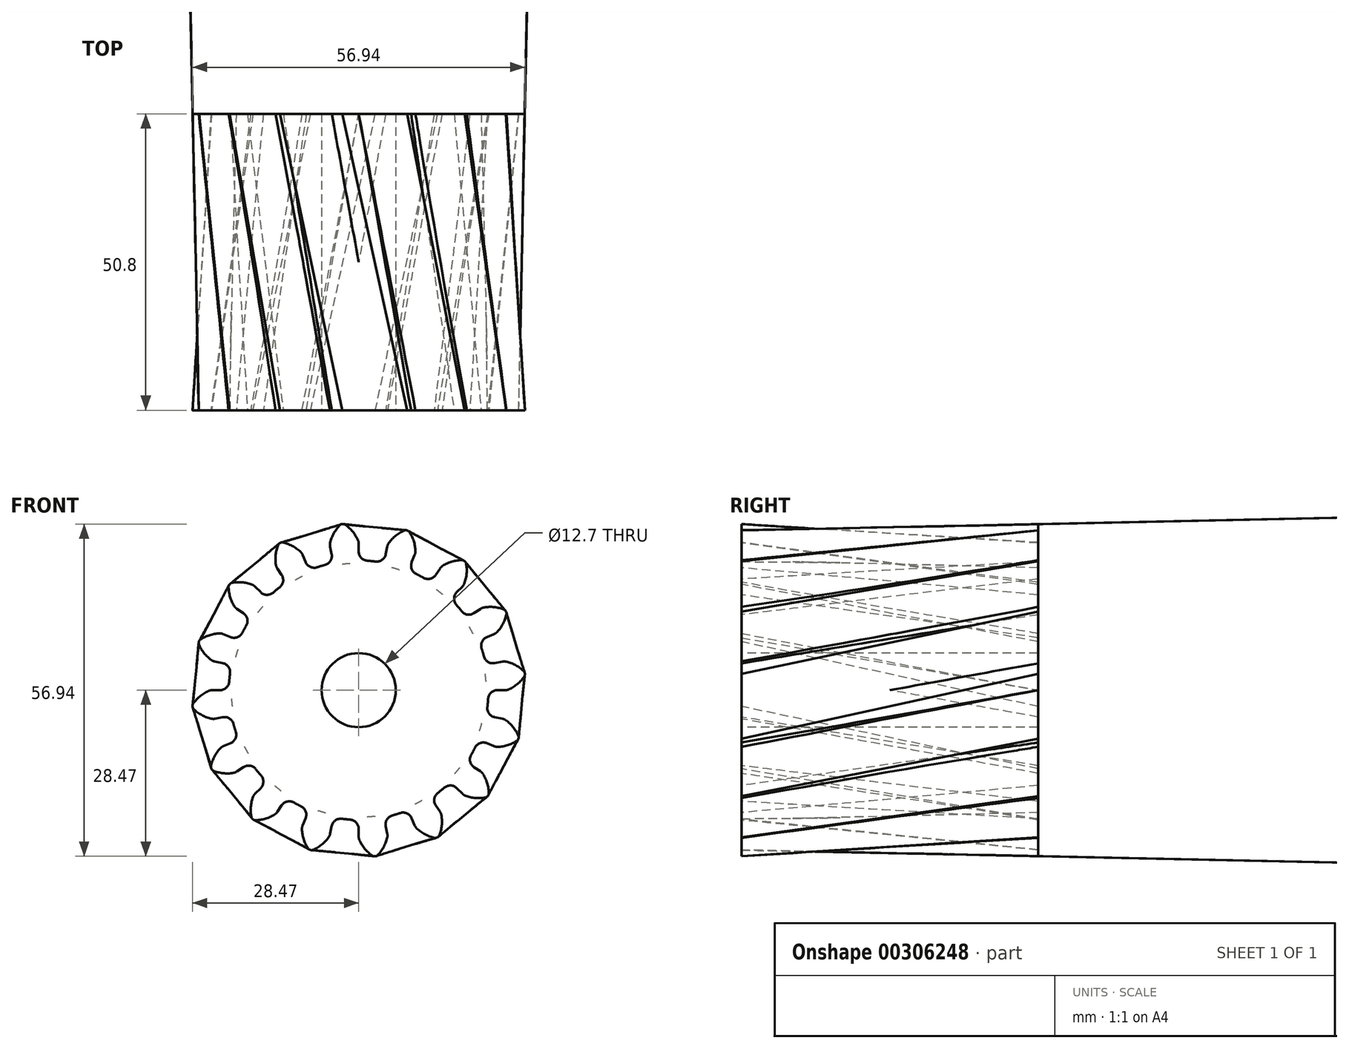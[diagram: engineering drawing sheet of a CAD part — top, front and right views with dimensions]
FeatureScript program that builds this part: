
annotation { "Feature Type Name" : "Feature", "Feature Type Description" : "" }
export const myFeature = defineFeature(function(context is Context, id is Id, definition is map)
    precondition{}
    {
        {
            var Q0;
            Q0=qCreatedBy(makeId("Front.planeOp"),FACE);
            var sketch = newSketch(context, id + "F0", { "sketchPlane" : qUnion([Q0])});
            skArc(sketch, "E0", {"start": v(-5.78, 21.46) * mm, "mid": v(-6.45, 21.27) * mm, "end": v(-7.12, 21.05) * mm});
            skArc(sketch, "E1.trimOffspring", {"start": v(-0.14, 25.74) * mm, "mid": v(-1.06, 27.2) * mm, "end": v(-2.34, 28.36) * mm});
            skLineSegment(sketch, "E2", {"start": v(-2.68, 28.45) * mm, "end": v(-2.8, 28.44) * mm});
            skLineSegment(sketch, "E3", {"start": v(0, 25.08) * mm, "end": v(0, 23.76) * mm});
            skLineSegment(sketch, "E4.MirrorCS", {"start": v(-4.9, 24.6) * mm, "end": v(-4.64, 23.3) * mm});
            skArc(sketch, "E5.MirrorCS", {"start": v(-4.88, 25.27) * mm, "mid": v(-4.27, 26.89) * mm, "end": v(-3.23, 28.28) * mm});
            skLineSegment(sketch, "E6.MirrorCS", {"start": v(-2.93, 28.43) * mm, "end": v(-2.8, 28.44) * mm});
            skPoint(sketch, "E7.visualSharp", {"position": v(-4.34, 21.8) * mm});
            skArc(sketch, "E7.filletArc", {"start": v(-5.78, 21.46) * mm, "mid": v(-4.84, 22.16) * mm, "end": v(-4.64, 23.3) * mm});
            skPoint(sketch, "E8.visualSharp", {"position": v(0, 22.23) * mm});
            skArc(sketch, "E8.filletArc", {"start": v(0, 23.76) * mm, "mid": v(0.43, 22.68) * mm, "end": v(1.48, 22.18) * mm});
            skPoint(sketch, "E9.visualSharp", {"position": v(-4.96, 24.91) * mm});
            skArc(sketch, "E9.filletArc", {"start": v(-4.88, 25.27) * mm, "mid": v(-4.92, 24.94) * mm, "end": v(-4.9, 24.6) * mm});
            skPoint(sketch, "E10.visualSharp", {"position": v(0, 25.4) * mm});
            skArc(sketch, "E10.filletArc", {"start": v(0, 25.08) * mm, "mid": v(-0.04, 25.42) * mm, "end": v(-0.14, 25.74) * mm});
            skPoint(sketch, "E11.visualSharp", {"position": v(-3.1, 28.4) * mm});
            skArc(sketch, "E11.filletArc", {"start": v(-2.93, 28.43) * mm, "mid": v(-3.1, 28.38) * mm, "end": v(-3.23, 28.28) * mm});
            skPoint(sketch, "E12.visualSharp", {"position": v(-2.5, 28.47) * mm});
            skArc(sketch, "E12.filletArc", {"start": v(-2.34, 28.36) * mm, "mid": v(-2.5, 28.44) * mm, "end": v(-2.68, 28.45) * mm});
            skPoint(sketch, "E13.1.0", {"position": v(-12.35, 18.48) * mm});
            skLineSegment(sketch, "E13.1.1", {"start": v(-9.6, 23.17) * mm, "end": v(-9.1, 21.95) * mm});
            skPoint(sketch, "E13.1.2", {"position": v(-13.2, 25.34) * mm});
            skArc(sketch, "E13.1.3", {"start": v(-14.18, 21.48) * mm, "mid": v(-14.23, 23.2) * mm, "end": v(-13.8, 24.89) * mm});
            skPoint(sketch, "E13.1.4", {"position": v(-13.74, 25.06) * mm});
            skPoint(sketch, "E13.1.5", {"position": v(-9.72, 23.47) * mm});
            skPoint(sketch, "E13.1.6", {"position": v(-14.11, 21.12) * mm});
            skPoint(sketch, "E13.1.7", {"position": v(-8.5, 20.53) * mm});
            skArc(sketch, "E13.1.8", {"start": v(-13.55, 17.62) * mm, "mid": v(-12.95, 18.62) * mm, "end": v(-13.2, 19.76) * mm});
            skArc(sketch, "E13.1.9", {"start": v(-9.98, 23.72) * mm, "mid": v(-11.4, 24.72) * mm, "end": v(-13.02, 25.3) * mm});
            skLineSegment(sketch, "E13.1.10", {"start": v(-13.94, 20.86) * mm, "end": v(-13.2, 19.76) * mm});
            skArc(sketch, "E13.1.11", {"start": v(-9.1, 21.95) * mm, "mid": v(-8.28, 21.11) * mm, "end": v(-7.12, 21.05) * mm});
            skArc(sketch, "E13.1.12", {"start": v(-14.18, 21.48) * mm, "mid": v(-14.1, 21.15) * mm, "end": v(-13.94, 20.86) * mm});
            skArc(sketch, "E13.1.13", {"start": v(-9.6, 23.17) * mm, "mid": v(-9.76, 23.47) * mm, "end": v(-9.98, 23.72) * mm});
            skArc(sketch, "E13.1.14", {"start": v(-13.58, 25.14) * mm, "mid": v(-13.72, 25.03) * mm, "end": v(-13.8, 24.89) * mm});
            skArc(sketch, "E13.1.15", {"start": v(-13.02, 25.3) * mm, "mid": v(-13.2, 25.31) * mm, "end": v(-13.36, 25.26) * mm});
            skLineSegment(sketch, "E13.1.16", {"start": v(-13.58, 25.14) * mm, "end": v(-13.47, 25.2) * mm});
            skLineSegment(sketch, "E13.1.17", {"start": v(-13.36, 25.26) * mm, "end": v(-13.47, 25.2) * mm});
            skPoint(sketch, "E13.2.0", {"position": v(-18.48, 12.35) * mm});
            skLineSegment(sketch, "E13.2.1", {"start": v(-17.74, 17.74) * mm, "end": v(-16.8, 16.8) * mm});
            skPoint(sketch, "E13.2.2", {"position": v(-21.9, 18.36) * mm});
            skArc(sketch, "E13.2.3", {"start": v(-21.32, 14.42) * mm, "mid": v(-22.03, 16) * mm, "end": v(-22.28, 17.7) * mm});
            skPoint(sketch, "E13.2.4", {"position": v(-22.28, 17.9) * mm});
            skPoint(sketch, "E13.2.5", {"position": v(-17.96, 17.96) * mm});
            skPoint(sketch, "E13.2.6", {"position": v(-21.12, 14.11) * mm});
            skPoint(sketch, "E13.2.7", {"position": v(-15.72, 15.72) * mm});
            skArc(sketch, "E13.2.8", {"start": v(-19.26, 11.09) * mm, "mid": v(-19.1, 12.24) * mm, "end": v(-19.76, 13.2) * mm});
            skArc(sketch, "E13.2.9", {"start": v(-18.3, 18.1) * mm, "mid": v(-19.99, 18.48) * mm, "end": v(-21.71, 18.4) * mm});
            skLineSegment(sketch, "E13.2.10", {"start": v(-20.86, 13.94) * mm, "end": v(-19.76, 13.2) * mm});
            skArc(sketch, "E13.2.11", {"start": v(-16.8, 16.8) * mm, "mid": v(-15.73, 16.34) * mm, "end": v(-14.63, 16.73) * mm});
            skArc(sketch, "E13.2.12", {"start": v(-21.32, 14.42) * mm, "mid": v(-21.11, 14.15) * mm, "end": v(-20.86, 13.94) * mm});
            skArc(sketch, "E13.2.13", {"start": v(-17.74, 17.74) * mm, "mid": v(-18, 17.95) * mm, "end": v(-18.3, 18.1) * mm});
            skArc(sketch, "E13.2.14", {"start": v(-22.17, 18.03) * mm, "mid": v(-22.25, 17.88) * mm, "end": v(-22.28, 17.7) * mm});
            skArc(sketch, "E13.2.15", {"start": v(-21.71, 18.4) * mm, "mid": v(-21.88, 18.34) * mm, "end": v(-22, 18.23) * mm});
            skLineSegment(sketch, "E13.2.16", {"start": v(-22.17, 18.03) * mm, "end": v(-22.1, 18.13) * mm});
            skLineSegment(sketch, "E13.2.17", {"start": v(-22, 18.23) * mm, "end": v(-22.1, 18.13) * mm});
            skLineSegment(sketch, "E14.1.3.0", {"start": v(-23.17, 9.6) * mm, "end": v(-21.95, 9.1) * mm});
            skPoint(sketch, "E14.4.3.0", {"position": v(-27.25, 8.59) * mm});
            skArc(sketch, "E14.5.3.0", {"start": v(-25.22, 5.16) * mm, "mid": v(-26.47, 6.35) * mm, "end": v(-27.36, 7.83) * mm});
            skPoint(sketch, "E14.9.3.0", {"position": v(-27.43, 8) * mm});
            skPoint(sketch, "E14.10.3.0", {"position": v(-23.47, 9.72) * mm});
            skPoint(sketch, "E14.11.3.0", {"position": v(-24.91, 4.96) * mm});
            skPoint(sketch, "E14.12.3.0", {"position": v(-20.53, 8.5) * mm});
            skArc(sketch, "E14.13.3.0", {"start": v(-22.04, 2.87) * mm, "mid": v(-22.32, 4) * mm, "end": v(-23.3, 4.64) * mm});
            skPoint(sketch, "E14.15.3.0", {"position": v(-21.8, 4.34) * mm});
            skArc(sketch, "E14.17.3.0", {"start": v(-23.83, 9.72) * mm, "mid": v(-25.54, 9.43) * mm, "end": v(-27.1, 8.69) * mm});
            skLineSegment(sketch, "E14.21.3.0", {"start": v(-24.6, 4.9) * mm, "end": v(-23.3, 4.64) * mm});
            skArc(sketch, "E14.24.3.0", {"start": v(-21.95, 9.1) * mm, "mid": v(-20.79, 9.07) * mm, "end": v(-19.92, 9.86) * mm});
            skArc(sketch, "E14.28.3.0", {"start": v(-25.22, 5.16) * mm, "mid": v(-24.92, 5) * mm, "end": v(-24.6, 4.9) * mm});
            skArc(sketch, "E14.32.3.0", {"start": v(-23.17, 9.6) * mm, "mid": v(-23.5, 9.7) * mm, "end": v(-23.83, 9.72) * mm});
            skArc(sketch, "E14.36.3.0", {"start": v(-27.38, 8.17) * mm, "mid": v(-27.4, 8) * mm, "end": v(-27.36, 7.83) * mm});
            skArc(sketch, "E14.40.3.0", {"start": v(-27.1, 8.69) * mm, "mid": v(-27.23, 8.57) * mm, "end": v(-27.3, 8.42) * mm});
            skLineSegment(sketch, "E14.44.3.0", {"start": v(-27.38, 8.17) * mm, "end": v(-27.35, 8.3) * mm});
            skLineSegment(sketch, "E14.47.3.0", {"start": v(-27.3, 8.42) * mm, "end": v(-27.35, 8.3) * mm});
            skLineSegment(sketch, "E14.1.4.0", {"start": v(-25.08, 0) * mm, "end": v(-23.76, 0) * mm});
            skPoint(sketch, "E14.4.4.0", {"position": v(-28.47, -2.5) * mm});
            skArc(sketch, "E14.5.4.0", {"start": v(-25.27, -4.88) * mm, "mid": v(-26.89, -4.27) * mm, "end": v(-28.28, -3.23) * mm});
            skPoint(sketch, "E14.9.4.0", {"position": v(-28.4, -3.1) * mm});
            skPoint(sketch, "E14.10.4.0", {"position": v(-25.4, 0) * mm});
            skPoint(sketch, "E14.11.4.0", {"position": v(-24.91, -4.96) * mm});
            skPoint(sketch, "E14.12.4.0", {"position": v(-22.23, 0) * mm});
            skArc(sketch, "E14.13.4.0", {"start": v(-21.46, -5.78) * mm, "mid": v(-22.16, -4.84) * mm, "end": v(-23.3, -4.64) * mm});
            skPoint(sketch, "E14.15.4.0", {"position": v(-21.8, -4.34) * mm});
            skArc(sketch, "E14.17.4.0", {"start": v(-25.74, -0.14) * mm, "mid": v(-27.2, -1.06) * mm, "end": v(-28.36, -2.34) * mm});
            skLineSegment(sketch, "E14.21.4.0", {"start": v(-24.6, -4.9) * mm, "end": v(-23.3, -4.64) * mm});
            skArc(sketch, "E14.24.4.0", {"start": v(-23.76, 0) * mm, "mid": v(-22.68, 0.43) * mm, "end": v(-22.18, 1.48) * mm});
            skArc(sketch, "E14.28.4.0", {"start": v(-25.27, -4.88) * mm, "mid": v(-24.94, -4.92) * mm, "end": v(-24.6, -4.9) * mm});
            skArc(sketch, "E14.32.4.0", {"start": v(-25.08, 0) * mm, "mid": v(-25.42, -0.04) * mm, "end": v(-25.74, -0.14) * mm});
            skArc(sketch, "E14.36.4.0", {"start": v(-28.43, -2.93) * mm, "mid": v(-28.38, -3.1) * mm, "end": v(-28.28, -3.23) * mm});
            skArc(sketch, "E14.40.4.0", {"start": v(-28.36, -2.34) * mm, "mid": v(-28.44, -2.5) * mm, "end": v(-28.45, -2.68) * mm});
            skLineSegment(sketch, "E14.44.4.0", {"start": v(-28.43, -2.93) * mm, "end": v(-28.44, -2.8) * mm});
            skLineSegment(sketch, "E14.47.4.0", {"start": v(-28.45, -2.68) * mm, "end": v(-28.44, -2.8) * mm});
            skLineSegment(sketch, "E14.1.5.0", {"start": v(-23.17, -9.6) * mm, "end": v(-21.95, -9.1) * mm});
            skPoint(sketch, "E14.4.5.0", {"position": v(-25.34, -13.2) * mm});
            skArc(sketch, "E14.5.5.0", {"start": v(-21.48, -14.18) * mm, "mid": v(-23.2, -14.23) * mm, "end": v(-24.89, -13.8) * mm});
            skPoint(sketch, "E14.9.5.0", {"position": v(-25.06, -13.74) * mm});
            skPoint(sketch, "E14.10.5.0", {"position": v(-23.47, -9.72) * mm});
            skPoint(sketch, "E14.11.5.0", {"position": v(-21.12, -14.11) * mm});
            skPoint(sketch, "E14.12.5.0", {"position": v(-20.53, -8.5) * mm});
            skArc(sketch, "E14.13.5.0", {"start": v(-17.62, -13.55) * mm, "mid": v(-18.62, -12.95) * mm, "end": v(-19.76, -13.2) * mm});
            skPoint(sketch, "E14.15.5.0", {"position": v(-18.48, -12.35) * mm});
            skArc(sketch, "E14.17.5.0", {"start": v(-23.72, -9.98) * mm, "mid": v(-24.72, -11.4) * mm, "end": v(-25.3, -13.02) * mm});
            skLineSegment(sketch, "E14.21.5.0", {"start": v(-20.86, -13.94) * mm, "end": v(-19.76, -13.2) * mm});
            skArc(sketch, "E14.24.5.0", {"start": v(-21.95, -9.1) * mm, "mid": v(-21.11, -8.28) * mm, "end": v(-21.05, -7.12) * mm});
            skArc(sketch, "E14.28.5.0", {"start": v(-21.48, -14.18) * mm, "mid": v(-21.15, -14.1) * mm, "end": v(-20.86, -13.94) * mm});
            skArc(sketch, "E14.32.5.0", {"start": v(-23.17, -9.6) * mm, "mid": v(-23.47, -9.76) * mm, "end": v(-23.72, -9.98) * mm});
            skArc(sketch, "E14.36.5.0", {"start": v(-25.14, -13.58) * mm, "mid": v(-25.03, -13.72) * mm, "end": v(-24.89, -13.8) * mm});
            skArc(sketch, "E14.40.5.0", {"start": v(-25.3, -13.02) * mm, "mid": v(-25.31, -13.2) * mm, "end": v(-25.26, -13.36) * mm});
            skLineSegment(sketch, "E14.44.5.0", {"start": v(-25.14, -13.58) * mm, "end": v(-25.2, -13.47) * mm});
            skLineSegment(sketch, "E14.47.5.0", {"start": v(-25.26, -13.36) * mm, "end": v(-25.2, -13.47) * mm});
            skLineSegment(sketch, "E14.1.6.0", {"start": v(-17.74, -17.74) * mm, "end": v(-16.8, -16.8) * mm});
            skPoint(sketch, "E14.4.6.0", {"position": v(-18.36, -21.9) * mm});
            skArc(sketch, "E14.5.6.0", {"start": v(-14.42, -21.32) * mm, "mid": v(-16, -22.03) * mm, "end": v(-17.7, -22.28) * mm});
            skPoint(sketch, "E14.9.6.0", {"position": v(-17.9, -22.28) * mm});
            skPoint(sketch, "E14.10.6.0", {"position": v(-17.96, -17.96) * mm});
            skPoint(sketch, "E14.11.6.0", {"position": v(-14.11, -21.12) * mm});
            skPoint(sketch, "E14.12.6.0", {"position": v(-15.72, -15.72) * mm});
            skArc(sketch, "E14.13.6.0", {"start": v(-11.09, -19.26) * mm, "mid": v(-12.24, -19.1) * mm, "end": v(-13.2, -19.76) * mm});
            skPoint(sketch, "E14.15.6.0", {"position": v(-12.35, -18.48) * mm});
            skArc(sketch, "E14.17.6.0", {"start": v(-18.1, -18.3) * mm, "mid": v(-18.48, -19.99) * mm, "end": v(-18.4, -21.71) * mm});
            skLineSegment(sketch, "E14.21.6.0", {"start": v(-13.94, -20.86) * mm, "end": v(-13.2, -19.76) * mm});
            skArc(sketch, "E14.24.6.0", {"start": v(-16.8, -16.8) * mm, "mid": v(-16.34, -15.73) * mm, "end": v(-16.73, -14.63) * mm});
            skArc(sketch, "E14.28.6.0", {"start": v(-14.42, -21.32) * mm, "mid": v(-14.15, -21.11) * mm, "end": v(-13.94, -20.86) * mm});
            skArc(sketch, "E14.32.6.0", {"start": v(-17.74, -17.74) * mm, "mid": v(-17.95, -18) * mm, "end": v(-18.1, -18.3) * mm});
            skArc(sketch, "E14.36.6.0", {"start": v(-18.03, -22.17) * mm, "mid": v(-17.88, -22.25) * mm, "end": v(-17.7, -22.28) * mm});
            skArc(sketch, "E14.40.6.0", {"start": v(-18.4, -21.71) * mm, "mid": v(-18.34, -21.88) * mm, "end": v(-18.23, -22) * mm});
            skLineSegment(sketch, "E14.44.6.0", {"start": v(-18.03, -22.17) * mm, "end": v(-18.13, -22.1) * mm});
            skLineSegment(sketch, "E14.47.6.0", {"start": v(-18.23, -22) * mm, "end": v(-18.13, -22.1) * mm});
            skLineSegment(sketch, "E14.1.7.0", {"start": v(-9.6, -23.17) * mm, "end": v(-9.1, -21.95) * mm});
            skPoint(sketch, "E14.4.7.0", {"position": v(-8.59, -27.25) * mm});
            skArc(sketch, "E14.5.7.0", {"start": v(-5.16, -25.22) * mm, "mid": v(-6.35, -26.47) * mm, "end": v(-7.83, -27.36) * mm});
            skPoint(sketch, "E14.9.7.0", {"position": v(-8, -27.43) * mm});
            skPoint(sketch, "E14.10.7.0", {"position": v(-9.72, -23.47) * mm});
            skPoint(sketch, "E14.11.7.0", {"position": v(-4.96, -24.91) * mm});
            skPoint(sketch, "E14.12.7.0", {"position": v(-8.5, -20.53) * mm});
            skArc(sketch, "E14.13.7.0", {"start": v(-2.87, -22.04) * mm, "mid": v(-4, -22.32) * mm, "end": v(-4.64, -23.3) * mm});
            skPoint(sketch, "E14.15.7.0", {"position": v(-4.34, -21.8) * mm});
            skArc(sketch, "E14.17.7.0", {"start": v(-9.72, -23.83) * mm, "mid": v(-9.43, -25.54) * mm, "end": v(-8.69, -27.1) * mm});
            skLineSegment(sketch, "E14.21.7.0", {"start": v(-4.9, -24.6) * mm, "end": v(-4.64, -23.3) * mm});
            skArc(sketch, "E14.24.7.0", {"start": v(-9.1, -21.95) * mm, "mid": v(-9.07, -20.79) * mm, "end": v(-9.86, -19.92) * mm});
            skArc(sketch, "E14.28.7.0", {"start": v(-5.16, -25.22) * mm, "mid": v(-5, -24.92) * mm, "end": v(-4.9, -24.6) * mm});
            skArc(sketch, "E14.32.7.0", {"start": v(-9.6, -23.17) * mm, "mid": v(-9.7, -23.5) * mm, "end": v(-9.72, -23.83) * mm});
            skArc(sketch, "E14.36.7.0", {"start": v(-8.17, -27.38) * mm, "mid": v(-8, -27.4) * mm, "end": v(-7.83, -27.36) * mm});
            skArc(sketch, "E14.40.7.0", {"start": v(-8.69, -27.1) * mm, "mid": v(-8.57, -27.23) * mm, "end": v(-8.42, -27.3) * mm});
            skLineSegment(sketch, "E14.44.7.0", {"start": v(-8.17, -27.38) * mm, "end": v(-8.3, -27.35) * mm});
            skLineSegment(sketch, "E14.47.7.0", {"start": v(-8.42, -27.3) * mm, "end": v(-8.3, -27.35) * mm});
            skLineSegment(sketch, "E14.1.8.0", {"start": v(0, -25.08) * mm, "end": v(0, -23.76) * mm});
            skPoint(sketch, "E14.4.8.0", {"position": v(2.5, -28.47) * mm});
            skArc(sketch, "E14.5.8.0", {"start": v(4.88, -25.27) * mm, "mid": v(4.27, -26.89) * mm, "end": v(3.23, -28.28) * mm});
            skPoint(sketch, "E14.9.8.0", {"position": v(3.1, -28.4) * mm});
            skPoint(sketch, "E14.10.8.0", {"position": v(0, -25.4) * mm});
            skPoint(sketch, "E14.11.8.0", {"position": v(4.96, -24.91) * mm});
            skPoint(sketch, "E14.12.8.0", {"position": v(0, -22.23) * mm});
            skArc(sketch, "E14.13.8.0", {"start": v(5.78, -21.46) * mm, "mid": v(4.84, -22.16) * mm, "end": v(4.64, -23.3) * mm});
            skPoint(sketch, "E14.15.8.0", {"position": v(4.34, -21.8) * mm});
            skArc(sketch, "E14.17.8.0", {"start": v(0.14, -25.74) * mm, "mid": v(1.06, -27.2) * mm, "end": v(2.34, -28.36) * mm});
            skLineSegment(sketch, "E14.21.8.0", {"start": v(4.9, -24.6) * mm, "end": v(4.64, -23.3) * mm});
            skArc(sketch, "E14.24.8.0", {"start": v(0, -23.76) * mm, "mid": v(-0.43, -22.68) * mm, "end": v(-1.48, -22.18) * mm});
            skArc(sketch, "E14.28.8.0", {"start": v(4.88, -25.27) * mm, "mid": v(4.92, -24.94) * mm, "end": v(4.9, -24.6) * mm});
            skArc(sketch, "E14.32.8.0", {"start": v(0, -25.08) * mm, "mid": v(0.04, -25.42) * mm, "end": v(0.14, -25.74) * mm});
            skArc(sketch, "E14.36.8.0", {"start": v(2.93, -28.43) * mm, "mid": v(3.1, -28.38) * mm, "end": v(3.23, -28.28) * mm});
            skArc(sketch, "E14.40.8.0", {"start": v(2.34, -28.36) * mm, "mid": v(2.5, -28.44) * mm, "end": v(2.68, -28.45) * mm});
            skLineSegment(sketch, "E14.44.8.0", {"start": v(2.93, -28.43) * mm, "end": v(2.8, -28.44) * mm});
            skLineSegment(sketch, "E14.47.8.0", {"start": v(2.68, -28.45) * mm, "end": v(2.8, -28.44) * mm});
            skLineSegment(sketch, "E14.1.9.0", {"start": v(9.6, -23.17) * mm, "end": v(9.1, -21.95) * mm});
            skPoint(sketch, "E14.4.9.0", {"position": v(13.2, -25.34) * mm});
            skArc(sketch, "E14.5.9.0", {"start": v(14.18, -21.48) * mm, "mid": v(14.23, -23.2) * mm, "end": v(13.8, -24.89) * mm});
            skPoint(sketch, "E14.9.9.0", {"position": v(13.74, -25.06) * mm});
            skPoint(sketch, "E14.10.9.0", {"position": v(9.72, -23.47) * mm});
            skPoint(sketch, "E14.11.9.0", {"position": v(14.11, -21.12) * mm});
            skPoint(sketch, "E14.12.9.0", {"position": v(8.5, -20.53) * mm});
            skArc(sketch, "E14.13.9.0", {"start": v(13.55, -17.62) * mm, "mid": v(12.95, -18.62) * mm, "end": v(13.2, -19.76) * mm});
            skPoint(sketch, "E14.15.9.0", {"position": v(12.35, -18.48) * mm});
            skArc(sketch, "E14.17.9.0", {"start": v(9.98, -23.72) * mm, "mid": v(11.4, -24.72) * mm, "end": v(13.02, -25.3) * mm});
            skLineSegment(sketch, "E14.21.9.0", {"start": v(13.94, -20.86) * mm, "end": v(13.2, -19.76) * mm});
            skArc(sketch, "E14.24.9.0", {"start": v(9.1, -21.95) * mm, "mid": v(8.28, -21.11) * mm, "end": v(7.12, -21.05) * mm});
            skArc(sketch, "E14.28.9.0", {"start": v(14.18, -21.48) * mm, "mid": v(14.1, -21.15) * mm, "end": v(13.94, -20.86) * mm});
            skArc(sketch, "E14.32.9.0", {"start": v(9.6, -23.17) * mm, "mid": v(9.76, -23.47) * mm, "end": v(9.98, -23.72) * mm});
            skArc(sketch, "E14.36.9.0", {"start": v(13.58, -25.14) * mm, "mid": v(13.72, -25.03) * mm, "end": v(13.8, -24.89) * mm});
            skArc(sketch, "E14.40.9.0", {"start": v(13.02, -25.3) * mm, "mid": v(13.2, -25.31) * mm, "end": v(13.36, -25.26) * mm});
            skLineSegment(sketch, "E14.44.9.0", {"start": v(13.58, -25.14) * mm, "end": v(13.47, -25.2) * mm});
            skLineSegment(sketch, "E14.47.9.0", {"start": v(13.36, -25.26) * mm, "end": v(13.47, -25.2) * mm});
            skLineSegment(sketch, "E14.1.10.0", {"start": v(17.74, -17.74) * mm, "end": v(16.8, -16.8) * mm});
            skPoint(sketch, "E14.4.10.0", {"position": v(21.9, -18.36) * mm});
            skArc(sketch, "E14.5.10.0", {"start": v(21.32, -14.42) * mm, "mid": v(22.03, -16) * mm, "end": v(22.28, -17.7) * mm});
            skPoint(sketch, "E14.9.10.0", {"position": v(22.28, -17.9) * mm});
            skPoint(sketch, "E14.10.10.0", {"position": v(17.96, -17.96) * mm});
            skPoint(sketch, "E14.11.10.0", {"position": v(21.12, -14.11) * mm});
            skPoint(sketch, "E14.12.10.0", {"position": v(15.72, -15.72) * mm});
            skArc(sketch, "E14.13.10.0", {"start": v(19.26, -11.09) * mm, "mid": v(19.1, -12.24) * mm, "end": v(19.76, -13.2) * mm});
            skPoint(sketch, "E14.15.10.0", {"position": v(18.48, -12.35) * mm});
            skArc(sketch, "E14.17.10.0", {"start": v(18.3, -18.1) * mm, "mid": v(19.99, -18.48) * mm, "end": v(21.71, -18.4) * mm});
            skLineSegment(sketch, "E14.21.10.0", {"start": v(20.86, -13.94) * mm, "end": v(19.76, -13.2) * mm});
            skArc(sketch, "E14.24.10.0", {"start": v(16.8, -16.8) * mm, "mid": v(15.73, -16.34) * mm, "end": v(14.63, -16.73) * mm});
            skArc(sketch, "E14.28.10.0", {"start": v(21.32, -14.42) * mm, "mid": v(21.11, -14.15) * mm, "end": v(20.86, -13.94) * mm});
            skArc(sketch, "E14.32.10.0", {"start": v(17.74, -17.74) * mm, "mid": v(18, -17.95) * mm, "end": v(18.3, -18.1) * mm});
            skArc(sketch, "E14.36.10.0", {"start": v(22.17, -18.03) * mm, "mid": v(22.25, -17.88) * mm, "end": v(22.28, -17.7) * mm});
            skArc(sketch, "E14.40.10.0", {"start": v(21.71, -18.4) * mm, "mid": v(21.88, -18.34) * mm, "end": v(22, -18.23) * mm});
            skLineSegment(sketch, "E14.44.10.0", {"start": v(22.17, -18.03) * mm, "end": v(22.1, -18.13) * mm});
            skLineSegment(sketch, "E14.47.10.0", {"start": v(22, -18.23) * mm, "end": v(22.1, -18.13) * mm});
            skLineSegment(sketch, "E14.1.11.0", {"start": v(23.17, -9.6) * mm, "end": v(21.95, -9.1) * mm});
            skPoint(sketch, "E14.4.11.0", {"position": v(27.25, -8.59) * mm});
            skArc(sketch, "E14.5.11.0", {"start": v(25.22, -5.16) * mm, "mid": v(26.47, -6.35) * mm, "end": v(27.36, -7.83) * mm});
            skPoint(sketch, "E14.9.11.0", {"position": v(27.43, -8) * mm});
            skPoint(sketch, "E14.10.11.0", {"position": v(23.47, -9.72) * mm});
            skPoint(sketch, "E14.11.11.0", {"position": v(24.91, -4.96) * mm});
            skPoint(sketch, "E14.12.11.0", {"position": v(20.53, -8.5) * mm});
            skArc(sketch, "E14.13.11.0", {"start": v(22.04, -2.87) * mm, "mid": v(22.32, -4) * mm, "end": v(23.3, -4.64) * mm});
            skPoint(sketch, "E14.15.11.0", {"position": v(21.8, -4.34) * mm});
            skArc(sketch, "E14.17.11.0", {"start": v(23.83, -9.72) * mm, "mid": v(25.54, -9.43) * mm, "end": v(27.1, -8.69) * mm});
            skLineSegment(sketch, "E14.21.11.0", {"start": v(24.6, -4.9) * mm, "end": v(23.3, -4.64) * mm});
            skArc(sketch, "E14.24.11.0", {"start": v(21.95, -9.1) * mm, "mid": v(20.79, -9.07) * mm, "end": v(19.92, -9.86) * mm});
            skArc(sketch, "E14.28.11.0", {"start": v(25.22, -5.16) * mm, "mid": v(24.92, -5) * mm, "end": v(24.6, -4.9) * mm});
            skArc(sketch, "E14.32.11.0", {"start": v(23.17, -9.6) * mm, "mid": v(23.5, -9.7) * mm, "end": v(23.83, -9.72) * mm});
            skArc(sketch, "E14.36.11.0", {"start": v(27.38, -8.17) * mm, "mid": v(27.4, -8) * mm, "end": v(27.36, -7.83) * mm});
            skArc(sketch, "E14.40.11.0", {"start": v(27.1, -8.69) * mm, "mid": v(27.23, -8.57) * mm, "end": v(27.3, -8.42) * mm});
            skLineSegment(sketch, "E14.44.11.0", {"start": v(27.38, -8.17) * mm, "end": v(27.35, -8.3) * mm});
            skLineSegment(sketch, "E14.47.11.0", {"start": v(27.3, -8.42) * mm, "end": v(27.35, -8.3) * mm});
            skLineSegment(sketch, "E14.1.12.0", {"start": v(25.08, 0) * mm, "end": v(23.76, 0) * mm});
            skPoint(sketch, "E14.4.12.0", {"position": v(28.47, 2.5) * mm});
            skArc(sketch, "E14.5.12.0", {"start": v(25.27, 4.88) * mm, "mid": v(26.89, 4.27) * mm, "end": v(28.28, 3.23) * mm});
            skPoint(sketch, "E14.9.12.0", {"position": v(28.4, 3.1) * mm});
            skPoint(sketch, "E14.10.12.0", {"position": v(25.4, 0) * mm});
            skPoint(sketch, "E14.11.12.0", {"position": v(24.91, 4.96) * mm});
            skPoint(sketch, "E14.12.12.0", {"position": v(22.23, 0) * mm});
            skArc(sketch, "E14.13.12.0", {"start": v(21.46, 5.78) * mm, "mid": v(22.16, 4.84) * mm, "end": v(23.3, 4.64) * mm});
            skPoint(sketch, "E14.15.12.0", {"position": v(21.8, 4.34) * mm});
            skArc(sketch, "E14.17.12.0", {"start": v(25.74, 0.14) * mm, "mid": v(27.2, 1.06) * mm, "end": v(28.36, 2.34) * mm});
            skLineSegment(sketch, "E14.21.12.0", {"start": v(24.6, 4.9) * mm, "end": v(23.3, 4.64) * mm});
            skArc(sketch, "E14.24.12.0", {"start": v(23.76, 0) * mm, "mid": v(22.68, -0.43) * mm, "end": v(22.18, -1.48) * mm});
            skArc(sketch, "E14.28.12.0", {"start": v(25.27, 4.88) * mm, "mid": v(24.94, 4.92) * mm, "end": v(24.6, 4.9) * mm});
            skArc(sketch, "E14.32.12.0", {"start": v(25.08, 0) * mm, "mid": v(25.42, 0.04) * mm, "end": v(25.74, 0.14) * mm});
            skArc(sketch, "E14.36.12.0", {"start": v(28.43, 2.93) * mm, "mid": v(28.38, 3.1) * mm, "end": v(28.28, 3.23) * mm});
            skArc(sketch, "E14.40.12.0", {"start": v(28.36, 2.34) * mm, "mid": v(28.44, 2.5) * mm, "end": v(28.45, 2.68) * mm});
            skLineSegment(sketch, "E14.44.12.0", {"start": v(28.43, 2.93) * mm, "end": v(28.44, 2.8) * mm});
            skLineSegment(sketch, "E14.47.12.0", {"start": v(28.45, 2.68) * mm, "end": v(28.44, 2.8) * mm});
            skLineSegment(sketch, "E14.1.13.0", {"start": v(23.17, 9.6) * mm, "end": v(21.95, 9.1) * mm});
            skPoint(sketch, "E14.4.13.0", {"position": v(25.34, 13.2) * mm});
            skArc(sketch, "E14.5.13.0", {"start": v(21.48, 14.18) * mm, "mid": v(23.2, 14.23) * mm, "end": v(24.89, 13.8) * mm});
            skPoint(sketch, "E14.9.13.0", {"position": v(25.06, 13.74) * mm});
            skPoint(sketch, "E14.10.13.0", {"position": v(23.47, 9.72) * mm});
            skPoint(sketch, "E14.11.13.0", {"position": v(21.12, 14.11) * mm});
            skPoint(sketch, "E14.12.13.0", {"position": v(20.53, 8.5) * mm});
            skArc(sketch, "E14.13.13.0", {"start": v(17.62, 13.55) * mm, "mid": v(18.62, 12.95) * mm, "end": v(19.76, 13.2) * mm});
            skPoint(sketch, "E14.15.13.0", {"position": v(18.48, 12.35) * mm});
            skArc(sketch, "E14.17.13.0", {"start": v(23.72, 9.98) * mm, "mid": v(24.72, 11.4) * mm, "end": v(25.3, 13.02) * mm});
            skLineSegment(sketch, "E14.21.13.0", {"start": v(20.86, 13.94) * mm, "end": v(19.76, 13.2) * mm});
            skArc(sketch, "E14.24.13.0", {"start": v(21.95, 9.1) * mm, "mid": v(21.11, 8.28) * mm, "end": v(21.05, 7.12) * mm});
            skArc(sketch, "E14.28.13.0", {"start": v(21.48, 14.18) * mm, "mid": v(21.15, 14.1) * mm, "end": v(20.86, 13.94) * mm});
            skArc(sketch, "E14.32.13.0", {"start": v(23.17, 9.6) * mm, "mid": v(23.47, 9.76) * mm, "end": v(23.72, 9.98) * mm});
            skArc(sketch, "E14.36.13.0", {"start": v(25.14, 13.58) * mm, "mid": v(25.03, 13.72) * mm, "end": v(24.89, 13.8) * mm});
            skArc(sketch, "E14.40.13.0", {"start": v(25.3, 13.02) * mm, "mid": v(25.31, 13.2) * mm, "end": v(25.26, 13.36) * mm});
            skLineSegment(sketch, "E14.44.13.0", {"start": v(25.14, 13.58) * mm, "end": v(25.2, 13.47) * mm});
            skLineSegment(sketch, "E14.47.13.0", {"start": v(25.26, 13.36) * mm, "end": v(25.2, 13.47) * mm});
            skLineSegment(sketch, "E14.1.14.0", {"start": v(17.74, 17.74) * mm, "end": v(16.8, 16.8) * mm});
            skPoint(sketch, "E14.4.14.0", {"position": v(18.36, 21.9) * mm});
            skArc(sketch, "E14.5.14.0", {"start": v(14.42, 21.32) * mm, "mid": v(16, 22.03) * mm, "end": v(17.7, 22.28) * mm});
            skPoint(sketch, "E14.9.14.0", {"position": v(17.9, 22.28) * mm});
            skPoint(sketch, "E14.10.14.0", {"position": v(17.96, 17.96) * mm});
            skPoint(sketch, "E14.11.14.0", {"position": v(14.11, 21.12) * mm});
            skPoint(sketch, "E14.12.14.0", {"position": v(15.72, 15.72) * mm});
            skArc(sketch, "E14.13.14.0", {"start": v(11.09, 19.26) * mm, "mid": v(12.24, 19.1) * mm, "end": v(13.2, 19.76) * mm});
            skPoint(sketch, "E14.15.14.0", {"position": v(12.35, 18.48) * mm});
            skArc(sketch, "E14.17.14.0", {"start": v(18.1, 18.3) * mm, "mid": v(18.48, 19.99) * mm, "end": v(18.4, 21.71) * mm});
            skLineSegment(sketch, "E14.21.14.0", {"start": v(13.94, 20.86) * mm, "end": v(13.2, 19.76) * mm});
            skArc(sketch, "E14.24.14.0", {"start": v(16.8, 16.8) * mm, "mid": v(16.34, 15.73) * mm, "end": v(16.73, 14.63) * mm});
            skArc(sketch, "E14.28.14.0", {"start": v(14.42, 21.32) * mm, "mid": v(14.15, 21.11) * mm, "end": v(13.94, 20.86) * mm});
            skArc(sketch, "E14.32.14.0", {"start": v(17.74, 17.74) * mm, "mid": v(17.95, 18) * mm, "end": v(18.1, 18.3) * mm});
            skArc(sketch, "E14.36.14.0", {"start": v(18.03, 22.17) * mm, "mid": v(17.88, 22.25) * mm, "end": v(17.7, 22.28) * mm});
            skArc(sketch, "E14.40.14.0", {"start": v(18.4, 21.71) * mm, "mid": v(18.34, 21.88) * mm, "end": v(18.23, 22) * mm});
            skLineSegment(sketch, "E14.44.14.0", {"start": v(18.03, 22.17) * mm, "end": v(18.13, 22.1) * mm});
            skLineSegment(sketch, "E14.47.14.0", {"start": v(18.23, 22) * mm, "end": v(18.13, 22.1) * mm});
            skLineSegment(sketch, "E14.1.15.0", {"start": v(9.6, 23.17) * mm, "end": v(9.1, 21.95) * mm});
            skPoint(sketch, "E14.4.15.0", {"position": v(8.59, 27.25) * mm});
            skArc(sketch, "E14.5.15.0", {"start": v(5.16, 25.22) * mm, "mid": v(6.35, 26.47) * mm, "end": v(7.83, 27.36) * mm});
            skPoint(sketch, "E14.9.15.0", {"position": v(8, 27.43) * mm});
            skPoint(sketch, "E14.10.15.0", {"position": v(9.72, 23.47) * mm});
            skPoint(sketch, "E14.11.15.0", {"position": v(4.96, 24.91) * mm});
            skPoint(sketch, "E14.12.15.0", {"position": v(8.5, 20.53) * mm});
            skArc(sketch, "E14.13.15.0", {"start": v(2.87, 22.04) * mm, "mid": v(4, 22.32) * mm, "end": v(4.64, 23.3) * mm});
            skPoint(sketch, "E14.15.15.0", {"position": v(4.34, 21.8) * mm});
            skArc(sketch, "E14.17.15.0", {"start": v(9.72, 23.83) * mm, "mid": v(9.43, 25.54) * mm, "end": v(8.69, 27.1) * mm});
            skLineSegment(sketch, "E14.21.15.0", {"start": v(4.9, 24.6) * mm, "end": v(4.64, 23.3) * mm});
            skArc(sketch, "E14.24.15.0", {"start": v(9.1, 21.95) * mm, "mid": v(9.07, 20.79) * mm, "end": v(9.86, 19.92) * mm});
            skArc(sketch, "E14.28.15.0", {"start": v(5.16, 25.22) * mm, "mid": v(5, 24.92) * mm, "end": v(4.9, 24.6) * mm});
            skArc(sketch, "E14.32.15.0", {"start": v(9.6, 23.17) * mm, "mid": v(9.7, 23.5) * mm, "end": v(9.72, 23.83) * mm});
            skArc(sketch, "E14.36.15.0", {"start": v(8.17, 27.38) * mm, "mid": v(8, 27.4) * mm, "end": v(7.83, 27.36) * mm});
            skArc(sketch, "E14.40.15.0", {"start": v(8.69, 27.1) * mm, "mid": v(8.57, 27.23) * mm, "end": v(8.42, 27.3) * mm});
            skLineSegment(sketch, "E14.44.15.0", {"start": v(8.17, 27.38) * mm, "end": v(8.3, 27.35) * mm});
            skLineSegment(sketch, "E14.47.15.0", {"start": v(8.42, 27.3) * mm, "end": v(8.3, 27.35) * mm});
            skArc(sketch, "E15.trimOffspring", {"start": v(2.87, 22.04) * mm, "mid": v(2.18, 22.12) * mm, "end": v(1.48, 22.18) * mm});
            skArc(sketch, "E16.trimOffspring", {"start": v(12.35, 18.48) * mm, "mid": v(11.12, 19.24) * mm, "end": v(9.86, 19.92) * mm});
            skArc(sketch, "E17.trimOffspring", {"start": v(17.62, 13.55) * mm, "mid": v(17.18, 14.1) * mm, "end": v(16.73, 14.63) * mm});
            skArc(sketch, "E18.trimOffspring", {"start": v(21.46, 5.78) * mm, "mid": v(21.27, 6.45) * mm, "end": v(21.05, 7.12) * mm});
            skArc(sketch, "E19.trimOffspring", {"start": v(22.04, -2.87) * mm, "mid": v(22.12, -2.18) * mm, "end": v(22.18, -1.48) * mm});
            skArc(sketch, "E20.trimOffspring", {"start": v(19.26, -11.09) * mm, "mid": v(19.6, -10.48) * mm, "end": v(19.92, -9.86) * mm});
            skArc(sketch, "E21.trimOffspring", {"start": v(13.55, -17.62) * mm, "mid": v(14.1, -17.18) * mm, "end": v(14.63, -16.73) * mm});
            skArc(sketch, "E22.trimOffspring", {"start": v(5.78, -21.46) * mm, "mid": v(6.45, -21.27) * mm, "end": v(7.12, -21.05) * mm});
            skArc(sketch, "E23.trimOffspring", {"start": v(-2.87, -22.04) * mm, "mid": v(-2.18, -22.12) * mm, "end": v(-1.48, -22.18) * mm});
            skArc(sketch, "E24.trimOffspring", {"start": v(-11.09, -19.26) * mm, "mid": v(-10.48, -19.6) * mm, "end": v(-9.86, -19.92) * mm});
            skArc(sketch, "E25.trimOffspring", {"start": v(-17.62, -13.55) * mm, "mid": v(-17.18, -14.1) * mm, "end": v(-16.73, -14.63) * mm});
            skArc(sketch, "E26.trimOffspring", {"start": v(-21.46, -5.78) * mm, "mid": v(-21.27, -6.45) * mm, "end": v(-21.05, -7.12) * mm});
            skArc(sketch, "E27.trimOffspring", {"start": v(-22.04, 2.87) * mm, "mid": v(-22.12, 2.18) * mm, "end": v(-22.18, 1.48) * mm});
            skArc(sketch, "E28.trimOffspring", {"start": v(-19.26, 11.09) * mm, "mid": v(-19.6, 10.48) * mm, "end": v(-19.92, 9.86) * mm});
            skArc(sketch, "E29.trimOffspring", {"start": v(-13.55, 17.62) * mm, "mid": v(-14.1, 17.18) * mm, "end": v(-14.63, 16.73) * mm});
            skSolve(sketch);
        }
        {
            var Q0;
            Q0=qCreatedBy(makeId("Front.planeOp"),FACE);
            cPlane(context, id + "F1", {"entities" : qUnion([Q0]), "cplaneType" : CPlaneType.OFFSET, "offset" : 50.8 * mm, "width" : 152.4 * mm, "height" : 152.4 * mm});
        }
        {
            var Q0;
            Q0=qCreatedBy(id+"F1.planeOp",FACE);
            var sketch = newSketch(context, id + "F2", { "sketchPlane" : qUnion([Q0])});
            skArc(sketch, "E30", {"start": v(-5.78, 21.46) * mm, "mid": v(-6.45, 21.27) * mm, "end": v(-7.12, 21.05) * mm});
            skArc(sketch, "E31.trimOffspring", {"start": v(-0.14, 25.74) * mm, "mid": v(-1.07, 27.21) * mm, "end": v(-2.37, 28.38) * mm});
            skLineSegment(sketch, "E32", {"start": v(-2.65, 28.47) * mm, "end": v(-2.8, 28.47) * mm});
            skLineSegment(sketch, "E33", {"start": v(0, 25.08) * mm, "end": v(0, 23.76) * mm});
            skLineSegment(sketch, "E34.MirrorCS", {"start": v(-2.95, 28.44) * mm, "end": v(-2.8, 28.47) * mm});
            skArc(sketch, "E35.MirrorCS", {"start": v(-4.88, 25.27) * mm, "mid": v(-4.26, 26.9) * mm, "end": v(-3.22, 28.3) * mm});
            skLineSegment(sketch, "E36.MirrorCS", {"start": v(-4.9, 24.6) * mm, "end": v(-4.64, 23.3) * mm});
            skPoint(sketch, "E37.visualSharp", {"position": v(-4.34, 21.8) * mm});
            skArc(sketch, "E37.filletArc", {"start": v(-4.7, 21.72) * mm, "mid": v(-4.46, 21.88) * mm, "end": v(-4.4, 22.16) * mm});
            skArc(sketch, "E38.filletArc", {"start": v(-5.78, 21.46) * mm, "mid": v(-4.84, 22.16) * mm, "end": v(-4.64, 23.3) * mm});
            skPoint(sketch, "E39.visualSharp", {"position": v(0, 22.23) * mm});
            skArc(sketch, "E39.filletArc", {"start": v(0, 23.76) * mm, "mid": v(0.43, 22.68) * mm, "end": v(1.48, 22.18) * mm});
            skPoint(sketch, "E40.visualSharp", {"position": v(-4.96, 24.91) * mm});
            skArc(sketch, "E40.filletArc", {"start": v(-4.88, 25.27) * mm, "mid": v(-4.92, 24.94) * mm, "end": v(-4.9, 24.6) * mm});
            skPoint(sketch, "E41.visualSharp", {"position": v(0, 25.4) * mm});
            skArc(sketch, "E41.filletArc", {"start": v(0, 25.08) * mm, "mid": v(-0.04, 25.42) * mm, "end": v(-0.14, 25.74) * mm});
            skPoint(sketch, "E42.visualSharp", {"position": v(-3.1, 28.4) * mm});
            skArc(sketch, "E42.filletArc", {"start": v(-2.95, 28.44) * mm, "mid": v(-3.1, 28.38) * mm, "end": v(-3.22, 28.3) * mm});
            skPoint(sketch, "E43.visualSharp", {"position": v(-2.5, 28.47) * mm});
            skArc(sketch, "E43.filletArc", {"start": v(-2.37, 28.38) * mm, "mid": v(-2.5, 28.44) * mm, "end": v(-2.65, 28.47) * mm});
            skArc(sketch, "E44.1.0", {"start": v(-13.55, 17.62) * mm, "mid": v(-12.95, 18.62) * mm, "end": v(-13.2, 19.76) * mm});
            skArc(sketch, "E44.1.1", {"start": v(-9.1, 21.95) * mm, "mid": v(-8.28, 21.11) * mm, "end": v(-7.12, 21.05) * mm});
            skPoint(sketch, "E44.1.2", {"position": v(-13.74, 25.06) * mm});
            skPoint(sketch, "E44.1.3", {"position": v(-14.11, 21.12) * mm});
            skPoint(sketch, "E44.1.4", {"position": v(-9.72, 23.47) * mm});
            skPoint(sketch, "E44.1.5", {"position": v(-13.2, 25.34) * mm});
            skLineSegment(sketch, "E44.1.6", {"start": v(-9.6, 23.17) * mm, "end": v(-9.1, 21.95) * mm});
            skArc(sketch, "E44.1.7", {"start": v(-9.98, 23.72) * mm, "mid": v(-11.4, 24.73) * mm, "end": v(-13.05, 25.31) * mm});
            skArc(sketch, "E44.1.8", {"start": v(-14.18, 21.48) * mm, "mid": v(-14.23, 23.22) * mm, "end": v(-13.8, 24.9) * mm});
            skLineSegment(sketch, "E44.1.9", {"start": v(-13.94, 20.86) * mm, "end": v(-13.2, 19.76) * mm});
            skArc(sketch, "E44.1.10", {"start": v(-9.6, 23.17) * mm, "mid": v(-9.76, 23.47) * mm, "end": v(-9.98, 23.72) * mm});
            skArc(sketch, "E44.1.11", {"start": v(-14.18, 21.48) * mm, "mid": v(-14.1, 21.15) * mm, "end": v(-13.94, 20.86) * mm});
            skArc(sketch, "E44.1.12", {"start": v(-13.05, 25.31) * mm, "mid": v(-13.2, 25.32) * mm, "end": v(-13.34, 25.28) * mm});
            skLineSegment(sketch, "E44.1.13", {"start": v(-13.61, 25.14) * mm, "end": v(-13.48, 25.23) * mm});
            skLineSegment(sketch, "E44.1.14", {"start": v(-13.34, 25.28) * mm, "end": v(-13.48, 25.23) * mm});
            skArc(sketch, "E44.1.15", {"start": v(-13.61, 25.14) * mm, "mid": v(-13.72, 25.04) * mm, "end": v(-13.8, 24.9) * mm});
            skArc(sketch, "E44.2.0", {"start": v(-19.26, 11.09) * mm, "mid": v(-19.1, 12.24) * mm, "end": v(-19.76, 13.2) * mm});
            skArc(sketch, "E44.2.1", {"start": v(-16.8, 16.8) * mm, "mid": v(-15.73, 16.34) * mm, "end": v(-14.63, 16.73) * mm});
            skPoint(sketch, "E44.2.2", {"position": v(-22.28, 17.9) * mm});
            skPoint(sketch, "E44.2.3", {"position": v(-21.12, 14.11) * mm});
            skPoint(sketch, "E44.2.4", {"position": v(-17.96, 17.96) * mm});
            skPoint(sketch, "E44.2.5", {"position": v(-21.9, 18.36) * mm});
            skLineSegment(sketch, "E44.2.6", {"start": v(-17.74, 17.74) * mm, "end": v(-16.8, 16.8) * mm});
            skArc(sketch, "E44.2.7", {"start": v(-18.3, 18.1) * mm, "mid": v(-20, 18.48) * mm, "end": v(-21.74, 18.4) * mm});
            skArc(sketch, "E44.2.8", {"start": v(-21.32, 14.42) * mm, "mid": v(-22.03, 16) * mm, "end": v(-22.28, 17.73) * mm});
            skLineSegment(sketch, "E44.2.9", {"start": v(-20.86, 13.94) * mm, "end": v(-19.76, 13.2) * mm});
            skArc(sketch, "E44.2.10", {"start": v(-17.74, 17.74) * mm, "mid": v(-18, 17.95) * mm, "end": v(-18.3, 18.1) * mm});
            skArc(sketch, "E44.2.11", {"start": v(-21.32, 14.42) * mm, "mid": v(-21.11, 14.15) * mm, "end": v(-20.86, 13.94) * mm});
            skArc(sketch, "E44.2.12", {"start": v(-21.74, 18.4) * mm, "mid": v(-21.88, 18.34) * mm, "end": v(-22, 18.25) * mm});
            skLineSegment(sketch, "E44.2.13", {"start": v(-22.2, 18.02) * mm, "end": v(-22.11, 18.15) * mm});
            skLineSegment(sketch, "E44.2.14", {"start": v(-22, 18.25) * mm, "end": v(-22.11, 18.15) * mm});
            skArc(sketch, "E44.2.15", {"start": v(-22.2, 18.02) * mm, "mid": v(-22.26, 17.88) * mm, "end": v(-22.28, 17.73) * mm});
            skArc(sketch, "E45.2.3.0", {"start": v(-22.04, 2.87) * mm, "mid": v(-22.32, 4) * mm, "end": v(-23.3, 4.64) * mm});
            skArc(sketch, "E45.4.3.0", {"start": v(-21.95, 9.1) * mm, "mid": v(-20.79, 9.07) * mm, "end": v(-19.92, 9.86) * mm});
            skPoint(sketch, "E45.8.3.0", {"position": v(-27.43, 8) * mm});
            skPoint(sketch, "E45.9.3.0", {"position": v(-24.91, 4.96) * mm});
            skPoint(sketch, "E45.10.3.0", {"position": v(-23.47, 9.72) * mm});
            skPoint(sketch, "E45.11.3.0", {"position": v(-27.25, 8.59) * mm});
            skLineSegment(sketch, "E45.12.3.0", {"start": v(-23.17, 9.6) * mm, "end": v(-21.95, 9.1) * mm});
            skArc(sketch, "E45.15.3.0", {"start": v(-23.83, 9.72) * mm, "mid": v(-25.55, 9.42) * mm, "end": v(-27.12, 8.67) * mm});
            skArc(sketch, "E45.19.3.0", {"start": v(-25.22, 5.16) * mm, "mid": v(-26.48, 6.36) * mm, "end": v(-27.37, 7.86) * mm});
            skLineSegment(sketch, "E45.23.3.0", {"start": v(-24.6, 4.9) * mm, "end": v(-23.3, 4.64) * mm});
            skArc(sketch, "E45.26.3.0", {"start": v(-23.17, 9.6) * mm, "mid": v(-23.5, 9.7) * mm, "end": v(-23.83, 9.72) * mm});
            skArc(sketch, "E45.30.3.0", {"start": v(-25.22, 5.16) * mm, "mid": v(-24.92, 5) * mm, "end": v(-24.6, 4.9) * mm});
            skArc(sketch, "E45.34.3.0", {"start": v(-27.12, 8.67) * mm, "mid": v(-27.24, 8.57) * mm, "end": v(-27.31, 8.44) * mm});
            skLineSegment(sketch, "E45.38.3.0", {"start": v(-27.4, 8.15) * mm, "end": v(-27.37, 8.3) * mm});
            skLineSegment(sketch, "E45.41.3.0", {"start": v(-27.31, 8.44) * mm, "end": v(-27.37, 8.3) * mm});
            skArc(sketch, "E45.44.3.0", {"start": v(-27.4, 8.15) * mm, "mid": v(-27.4, 8) * mm, "end": v(-27.37, 7.86) * mm});
            skArc(sketch, "E45.2.4.0", {"start": v(-21.46, -5.78) * mm, "mid": v(-22.16, -4.84) * mm, "end": v(-23.3, -4.64) * mm});
            skArc(sketch, "E45.4.4.0", {"start": v(-23.76, 0) * mm, "mid": v(-22.68, 0.43) * mm, "end": v(-22.18, 1.48) * mm});
            skPoint(sketch, "E45.8.4.0", {"position": v(-28.4, -3.1) * mm});
            skPoint(sketch, "E45.9.4.0", {"position": v(-24.91, -4.96) * mm});
            skPoint(sketch, "E45.10.4.0", {"position": v(-25.4, 0) * mm});
            skPoint(sketch, "E45.11.4.0", {"position": v(-28.47, -2.5) * mm});
            skLineSegment(sketch, "E45.12.4.0", {"start": v(-25.08, 0) * mm, "end": v(-23.76, 0) * mm});
            skArc(sketch, "E45.15.4.0", {"start": v(-25.74, -0.14) * mm, "mid": v(-27.21, -1.07) * mm, "end": v(-28.38, -2.37) * mm});
            skArc(sketch, "E45.19.4.0", {"start": v(-25.27, -4.88) * mm, "mid": v(-26.9, -4.26) * mm, "end": v(-28.3, -3.22) * mm});
            skLineSegment(sketch, "E45.23.4.0", {"start": v(-24.6, -4.9) * mm, "end": v(-23.3, -4.64) * mm});
            skArc(sketch, "E45.26.4.0", {"start": v(-25.08, 0) * mm, "mid": v(-25.42, -0.04) * mm, "end": v(-25.74, -0.14) * mm});
            skArc(sketch, "E45.30.4.0", {"start": v(-25.27, -4.88) * mm, "mid": v(-24.94, -4.92) * mm, "end": v(-24.6, -4.9) * mm});
            skArc(sketch, "E45.34.4.0", {"start": v(-28.38, -2.37) * mm, "mid": v(-28.44, -2.5) * mm, "end": v(-28.47, -2.65) * mm});
            skLineSegment(sketch, "E45.38.4.0", {"start": v(-28.44, -2.95) * mm, "end": v(-28.47, -2.8) * mm});
            skLineSegment(sketch, "E45.41.4.0", {"start": v(-28.47, -2.65) * mm, "end": v(-28.47, -2.8) * mm});
            skArc(sketch, "E45.44.4.0", {"start": v(-28.44, -2.95) * mm, "mid": v(-28.38, -3.1) * mm, "end": v(-28.3, -3.22) * mm});
            skArc(sketch, "E45.2.5.0", {"start": v(-17.62, -13.55) * mm, "mid": v(-18.62, -12.95) * mm, "end": v(-19.76, -13.2) * mm});
            skArc(sketch, "E45.4.5.0", {"start": v(-21.95, -9.1) * mm, "mid": v(-21.11, -8.28) * mm, "end": v(-21.05, -7.12) * mm});
            skPoint(sketch, "E45.8.5.0", {"position": v(-25.06, -13.74) * mm});
            skPoint(sketch, "E45.9.5.0", {"position": v(-21.12, -14.11) * mm});
            skPoint(sketch, "E45.10.5.0", {"position": v(-23.47, -9.72) * mm});
            skPoint(sketch, "E45.11.5.0", {"position": v(-25.34, -13.2) * mm});
            skLineSegment(sketch, "E45.12.5.0", {"start": v(-23.17, -9.6) * mm, "end": v(-21.95, -9.1) * mm});
            skArc(sketch, "E45.15.5.0", {"start": v(-23.72, -9.98) * mm, "mid": v(-24.73, -11.4) * mm, "end": v(-25.31, -13.05) * mm});
            skArc(sketch, "E45.19.5.0", {"start": v(-21.48, -14.18) * mm, "mid": v(-23.22, -14.23) * mm, "end": v(-24.9, -13.8) * mm});
            skLineSegment(sketch, "E45.23.5.0", {"start": v(-20.86, -13.94) * mm, "end": v(-19.76, -13.2) * mm});
            skArc(sketch, "E45.26.5.0", {"start": v(-23.17, -9.6) * mm, "mid": v(-23.47, -9.76) * mm, "end": v(-23.72, -9.98) * mm});
            skArc(sketch, "E45.30.5.0", {"start": v(-21.48, -14.18) * mm, "mid": v(-21.15, -14.1) * mm, "end": v(-20.86, -13.94) * mm});
            skArc(sketch, "E45.34.5.0", {"start": v(-25.31, -13.05) * mm, "mid": v(-25.32, -13.2) * mm, "end": v(-25.28, -13.34) * mm});
            skLineSegment(sketch, "E45.38.5.0", {"start": v(-25.14, -13.61) * mm, "end": v(-25.23, -13.48) * mm});
            skLineSegment(sketch, "E45.41.5.0", {"start": v(-25.28, -13.34) * mm, "end": v(-25.23, -13.48) * mm});
            skArc(sketch, "E45.44.5.0", {"start": v(-25.14, -13.61) * mm, "mid": v(-25.04, -13.72) * mm, "end": v(-24.9, -13.8) * mm});
            skArc(sketch, "E45.2.6.0", {"start": v(-11.09, -19.26) * mm, "mid": v(-12.24, -19.1) * mm, "end": v(-13.2, -19.76) * mm});
            skArc(sketch, "E45.4.6.0", {"start": v(-16.8, -16.8) * mm, "mid": v(-16.34, -15.73) * mm, "end": v(-16.73, -14.63) * mm});
            skPoint(sketch, "E45.8.6.0", {"position": v(-17.9, -22.28) * mm});
            skPoint(sketch, "E45.9.6.0", {"position": v(-14.11, -21.12) * mm});
            skPoint(sketch, "E45.10.6.0", {"position": v(-17.96, -17.96) * mm});
            skPoint(sketch, "E45.11.6.0", {"position": v(-18.36, -21.9) * mm});
            skLineSegment(sketch, "E45.12.6.0", {"start": v(-17.74, -17.74) * mm, "end": v(-16.8, -16.8) * mm});
            skArc(sketch, "E45.15.6.0", {"start": v(-18.1, -18.3) * mm, "mid": v(-18.48, -20) * mm, "end": v(-18.4, -21.74) * mm});
            skArc(sketch, "E45.19.6.0", {"start": v(-14.42, -21.32) * mm, "mid": v(-16, -22.03) * mm, "end": v(-17.73, -22.28) * mm});
            skLineSegment(sketch, "E45.23.6.0", {"start": v(-13.94, -20.86) * mm, "end": v(-13.2, -19.76) * mm});
            skArc(sketch, "E45.26.6.0", {"start": v(-17.74, -17.74) * mm, "mid": v(-17.95, -18) * mm, "end": v(-18.1, -18.3) * mm});
            skArc(sketch, "E45.30.6.0", {"start": v(-14.42, -21.32) * mm, "mid": v(-14.15, -21.11) * mm, "end": v(-13.94, -20.86) * mm});
            skArc(sketch, "E45.34.6.0", {"start": v(-18.4, -21.74) * mm, "mid": v(-18.34, -21.88) * mm, "end": v(-18.25, -22) * mm});
            skLineSegment(sketch, "E45.38.6.0", {"start": v(-18.02, -22.2) * mm, "end": v(-18.15, -22.11) * mm});
            skLineSegment(sketch, "E45.41.6.0", {"start": v(-18.25, -22) * mm, "end": v(-18.15, -22.11) * mm});
            skArc(sketch, "E45.44.6.0", {"start": v(-18.02, -22.2) * mm, "mid": v(-17.88, -22.26) * mm, "end": v(-17.73, -22.28) * mm});
            skArc(sketch, "E45.2.7.0", {"start": v(-2.87, -22.04) * mm, "mid": v(-4, -22.32) * mm, "end": v(-4.64, -23.3) * mm});
            skArc(sketch, "E45.4.7.0", {"start": v(-9.1, -21.95) * mm, "mid": v(-9.07, -20.79) * mm, "end": v(-9.86, -19.92) * mm});
            skPoint(sketch, "E45.8.7.0", {"position": v(-8, -27.43) * mm});
            skPoint(sketch, "E45.9.7.0", {"position": v(-4.96, -24.91) * mm});
            skPoint(sketch, "E45.10.7.0", {"position": v(-9.72, -23.47) * mm});
            skPoint(sketch, "E45.11.7.0", {"position": v(-8.59, -27.25) * mm});
            skLineSegment(sketch, "E45.12.7.0", {"start": v(-9.6, -23.17) * mm, "end": v(-9.1, -21.95) * mm});
            skArc(sketch, "E45.15.7.0", {"start": v(-9.72, -23.83) * mm, "mid": v(-9.42, -25.55) * mm, "end": v(-8.67, -27.12) * mm});
            skArc(sketch, "E45.19.7.0", {"start": v(-5.16, -25.22) * mm, "mid": v(-6.36, -26.48) * mm, "end": v(-7.86, -27.37) * mm});
            skLineSegment(sketch, "E45.23.7.0", {"start": v(-4.9, -24.6) * mm, "end": v(-4.64, -23.3) * mm});
            skArc(sketch, "E45.26.7.0", {"start": v(-9.6, -23.17) * mm, "mid": v(-9.7, -23.5) * mm, "end": v(-9.72, -23.83) * mm});
            skArc(sketch, "E45.30.7.0", {"start": v(-5.16, -25.22) * mm, "mid": v(-5, -24.92) * mm, "end": v(-4.9, -24.6) * mm});
            skArc(sketch, "E45.34.7.0", {"start": v(-8.67, -27.12) * mm, "mid": v(-8.57, -27.24) * mm, "end": v(-8.44, -27.31) * mm});
            skLineSegment(sketch, "E45.38.7.0", {"start": v(-8.15, -27.4) * mm, "end": v(-8.3, -27.37) * mm});
            skLineSegment(sketch, "E45.41.7.0", {"start": v(-8.44, -27.31) * mm, "end": v(-8.3, -27.37) * mm});
            skArc(sketch, "E45.44.7.0", {"start": v(-8.15, -27.4) * mm, "mid": v(-8, -27.4) * mm, "end": v(-7.86, -27.37) * mm});
            skArc(sketch, "E45.2.8.0", {"start": v(5.78, -21.46) * mm, "mid": v(4.84, -22.16) * mm, "end": v(4.64, -23.3) * mm});
            skArc(sketch, "E45.4.8.0", {"start": v(0, -23.76) * mm, "mid": v(-0.43, -22.68) * mm, "end": v(-1.48, -22.18) * mm});
            skPoint(sketch, "E45.8.8.0", {"position": v(3.1, -28.4) * mm});
            skPoint(sketch, "E45.9.8.0", {"position": v(4.96, -24.91) * mm});
            skPoint(sketch, "E45.10.8.0", {"position": v(0, -25.4) * mm});
            skPoint(sketch, "E45.11.8.0", {"position": v(2.5, -28.47) * mm});
            skLineSegment(sketch, "E45.12.8.0", {"start": v(0, -25.08) * mm, "end": v(0, -23.76) * mm});
            skArc(sketch, "E45.15.8.0", {"start": v(0.14, -25.74) * mm, "mid": v(1.07, -27.21) * mm, "end": v(2.37, -28.38) * mm});
            skArc(sketch, "E45.19.8.0", {"start": v(4.88, -25.27) * mm, "mid": v(4.26, -26.9) * mm, "end": v(3.22, -28.3) * mm});
            skLineSegment(sketch, "E45.23.8.0", {"start": v(4.9, -24.6) * mm, "end": v(4.64, -23.3) * mm});
            skArc(sketch, "E45.26.8.0", {"start": v(0, -25.08) * mm, "mid": v(0.04, -25.42) * mm, "end": v(0.14, -25.74) * mm});
            skArc(sketch, "E45.30.8.0", {"start": v(4.88, -25.27) * mm, "mid": v(4.92, -24.94) * mm, "end": v(4.9, -24.6) * mm});
            skArc(sketch, "E45.34.8.0", {"start": v(2.37, -28.38) * mm, "mid": v(2.5, -28.44) * mm, "end": v(2.65, -28.47) * mm});
            skLineSegment(sketch, "E45.38.8.0", {"start": v(2.95, -28.44) * mm, "end": v(2.8, -28.47) * mm});
            skLineSegment(sketch, "E45.41.8.0", {"start": v(2.65, -28.47) * mm, "end": v(2.8, -28.47) * mm});
            skArc(sketch, "E45.44.8.0", {"start": v(2.95, -28.44) * mm, "mid": v(3.1, -28.38) * mm, "end": v(3.22, -28.3) * mm});
            skArc(sketch, "E45.2.9.0", {"start": v(13.55, -17.62) * mm, "mid": v(12.95, -18.62) * mm, "end": v(13.2, -19.76) * mm});
            skArc(sketch, "E45.4.9.0", {"start": v(9.1, -21.95) * mm, "mid": v(8.28, -21.11) * mm, "end": v(7.12, -21.05) * mm});
            skPoint(sketch, "E45.8.9.0", {"position": v(13.74, -25.06) * mm});
            skPoint(sketch, "E45.9.9.0", {"position": v(14.11, -21.12) * mm});
            skPoint(sketch, "E45.10.9.0", {"position": v(9.72, -23.47) * mm});
            skPoint(sketch, "E45.11.9.0", {"position": v(13.2, -25.34) * mm});
            skLineSegment(sketch, "E45.12.9.0", {"start": v(9.6, -23.17) * mm, "end": v(9.1, -21.95) * mm});
            skArc(sketch, "E45.15.9.0", {"start": v(9.98, -23.72) * mm, "mid": v(11.4, -24.73) * mm, "end": v(13.05, -25.31) * mm});
            skArc(sketch, "E45.19.9.0", {"start": v(14.18, -21.48) * mm, "mid": v(14.23, -23.22) * mm, "end": v(13.8, -24.9) * mm});
            skLineSegment(sketch, "E45.23.9.0", {"start": v(13.94, -20.86) * mm, "end": v(13.2, -19.76) * mm});
            skArc(sketch, "E45.26.9.0", {"start": v(9.6, -23.17) * mm, "mid": v(9.76, -23.47) * mm, "end": v(9.98, -23.72) * mm});
            skArc(sketch, "E45.30.9.0", {"start": v(14.18, -21.48) * mm, "mid": v(14.1, -21.15) * mm, "end": v(13.94, -20.86) * mm});
            skArc(sketch, "E45.34.9.0", {"start": v(13.05, -25.31) * mm, "mid": v(13.2, -25.32) * mm, "end": v(13.34, -25.28) * mm});
            skLineSegment(sketch, "E45.38.9.0", {"start": v(13.61, -25.14) * mm, "end": v(13.48, -25.23) * mm});
            skLineSegment(sketch, "E45.41.9.0", {"start": v(13.34, -25.28) * mm, "end": v(13.48, -25.23) * mm});
            skArc(sketch, "E45.44.9.0", {"start": v(13.61, -25.14) * mm, "mid": v(13.72, -25.04) * mm, "end": v(13.8, -24.9) * mm});
            skArc(sketch, "E45.2.10.0", {"start": v(19.26, -11.09) * mm, "mid": v(19.1, -12.24) * mm, "end": v(19.76, -13.2) * mm});
            skArc(sketch, "E45.4.10.0", {"start": v(16.8, -16.8) * mm, "mid": v(15.73, -16.34) * mm, "end": v(14.63, -16.73) * mm});
            skPoint(sketch, "E45.8.10.0", {"position": v(22.28, -17.9) * mm});
            skPoint(sketch, "E45.9.10.0", {"position": v(21.12, -14.11) * mm});
            skPoint(sketch, "E45.10.10.0", {"position": v(17.96, -17.96) * mm});
            skPoint(sketch, "E45.11.10.0", {"position": v(21.9, -18.36) * mm});
            skLineSegment(sketch, "E45.12.10.0", {"start": v(17.74, -17.74) * mm, "end": v(16.8, -16.8) * mm});
            skArc(sketch, "E45.15.10.0", {"start": v(18.3, -18.1) * mm, "mid": v(20, -18.48) * mm, "end": v(21.74, -18.4) * mm});
            skArc(sketch, "E45.19.10.0", {"start": v(21.32, -14.42) * mm, "mid": v(22.03, -16) * mm, "end": v(22.28, -17.73) * mm});
            skLineSegment(sketch, "E45.23.10.0", {"start": v(20.86, -13.94) * mm, "end": v(19.76, -13.2) * mm});
            skArc(sketch, "E45.26.10.0", {"start": v(17.74, -17.74) * mm, "mid": v(18, -17.95) * mm, "end": v(18.3, -18.1) * mm});
            skArc(sketch, "E45.30.10.0", {"start": v(21.32, -14.42) * mm, "mid": v(21.11, -14.15) * mm, "end": v(20.86, -13.94) * mm});
            skArc(sketch, "E45.34.10.0", {"start": v(21.74, -18.4) * mm, "mid": v(21.88, -18.34) * mm, "end": v(22, -18.25) * mm});
            skLineSegment(sketch, "E45.38.10.0", {"start": v(22.2, -18.02) * mm, "end": v(22.11, -18.15) * mm});
            skLineSegment(sketch, "E45.41.10.0", {"start": v(22, -18.25) * mm, "end": v(22.11, -18.15) * mm});
            skArc(sketch, "E45.44.10.0", {"start": v(22.2, -18.02) * mm, "mid": v(22.26, -17.88) * mm, "end": v(22.28, -17.73) * mm});
            skArc(sketch, "E45.2.11.0", {"start": v(22.04, -2.87) * mm, "mid": v(22.32, -4) * mm, "end": v(23.3, -4.64) * mm});
            skArc(sketch, "E45.4.11.0", {"start": v(21.95, -9.1) * mm, "mid": v(20.79, -9.07) * mm, "end": v(19.92, -9.86) * mm});
            skPoint(sketch, "E45.8.11.0", {"position": v(27.43, -8) * mm});
            skPoint(sketch, "E45.9.11.0", {"position": v(24.91, -4.96) * mm});
            skPoint(sketch, "E45.10.11.0", {"position": v(23.47, -9.72) * mm});
            skPoint(sketch, "E45.11.11.0", {"position": v(27.25, -8.59) * mm});
            skLineSegment(sketch, "E45.12.11.0", {"start": v(23.17, -9.6) * mm, "end": v(21.95, -9.1) * mm});
            skArc(sketch, "E45.15.11.0", {"start": v(23.83, -9.72) * mm, "mid": v(25.55, -9.42) * mm, "end": v(27.12, -8.67) * mm});
            skArc(sketch, "E45.19.11.0", {"start": v(25.22, -5.16) * mm, "mid": v(26.48, -6.36) * mm, "end": v(27.37, -7.86) * mm});
            skLineSegment(sketch, "E45.23.11.0", {"start": v(24.6, -4.9) * mm, "end": v(23.3, -4.64) * mm});
            skArc(sketch, "E45.26.11.0", {"start": v(23.17, -9.6) * mm, "mid": v(23.5, -9.7) * mm, "end": v(23.83, -9.72) * mm});
            skArc(sketch, "E45.30.11.0", {"start": v(25.22, -5.16) * mm, "mid": v(24.92, -5) * mm, "end": v(24.6, -4.9) * mm});
            skArc(sketch, "E45.34.11.0", {"start": v(27.12, -8.67) * mm, "mid": v(27.24, -8.57) * mm, "end": v(27.31, -8.44) * mm});
            skLineSegment(sketch, "E45.38.11.0", {"start": v(27.4, -8.15) * mm, "end": v(27.37, -8.3) * mm});
            skLineSegment(sketch, "E45.41.11.0", {"start": v(27.31, -8.44) * mm, "end": v(27.37, -8.3) * mm});
            skArc(sketch, "E45.44.11.0", {"start": v(27.4, -8.15) * mm, "mid": v(27.4, -8) * mm, "end": v(27.37, -7.86) * mm});
            skArc(sketch, "E45.2.12.0", {"start": v(21.46, 5.78) * mm, "mid": v(22.16, 4.84) * mm, "end": v(23.3, 4.64) * mm});
            skArc(sketch, "E45.4.12.0", {"start": v(23.76, 0) * mm, "mid": v(22.68, -0.43) * mm, "end": v(22.18, -1.48) * mm});
            skPoint(sketch, "E45.8.12.0", {"position": v(28.4, 3.1) * mm});
            skPoint(sketch, "E45.9.12.0", {"position": v(24.91, 4.96) * mm});
            skPoint(sketch, "E45.10.12.0", {"position": v(25.4, 0) * mm});
            skPoint(sketch, "E45.11.12.0", {"position": v(28.47, 2.5) * mm});
            skLineSegment(sketch, "E45.12.12.0", {"start": v(25.08, 0) * mm, "end": v(23.76, 0) * mm});
            skArc(sketch, "E45.15.12.0", {"start": v(25.74, 0.14) * mm, "mid": v(27.21, 1.07) * mm, "end": v(28.38, 2.37) * mm});
            skArc(sketch, "E45.19.12.0", {"start": v(25.27, 4.88) * mm, "mid": v(26.9, 4.26) * mm, "end": v(28.3, 3.22) * mm});
            skLineSegment(sketch, "E45.23.12.0", {"start": v(24.6, 4.9) * mm, "end": v(23.3, 4.64) * mm});
            skArc(sketch, "E45.26.12.0", {"start": v(25.08, 0) * mm, "mid": v(25.42, 0.04) * mm, "end": v(25.74, 0.14) * mm});
            skArc(sketch, "E45.30.12.0", {"start": v(25.27, 4.88) * mm, "mid": v(24.94, 4.92) * mm, "end": v(24.6, 4.9) * mm});
            skArc(sketch, "E45.34.12.0", {"start": v(28.38, 2.37) * mm, "mid": v(28.44, 2.5) * mm, "end": v(28.47, 2.65) * mm});
            skLineSegment(sketch, "E45.38.12.0", {"start": v(28.44, 2.95) * mm, "end": v(28.47, 2.8) * mm});
            skLineSegment(sketch, "E45.41.12.0", {"start": v(28.47, 2.65) * mm, "end": v(28.47, 2.8) * mm});
            skArc(sketch, "E45.44.12.0", {"start": v(28.44, 2.95) * mm, "mid": v(28.38, 3.1) * mm, "end": v(28.3, 3.22) * mm});
            skArc(sketch, "E45.2.13.0", {"start": v(17.62, 13.55) * mm, "mid": v(18.62, 12.95) * mm, "end": v(19.76, 13.2) * mm});
            skArc(sketch, "E45.4.13.0", {"start": v(21.95, 9.1) * mm, "mid": v(21.11, 8.28) * mm, "end": v(21.05, 7.12) * mm});
            skPoint(sketch, "E45.8.13.0", {"position": v(25.06, 13.74) * mm});
            skPoint(sketch, "E45.9.13.0", {"position": v(21.12, 14.11) * mm});
            skPoint(sketch, "E45.10.13.0", {"position": v(23.47, 9.72) * mm});
            skPoint(sketch, "E45.11.13.0", {"position": v(25.34, 13.2) * mm});
            skLineSegment(sketch, "E45.12.13.0", {"start": v(23.17, 9.6) * mm, "end": v(21.95, 9.1) * mm});
            skArc(sketch, "E45.15.13.0", {"start": v(23.72, 9.98) * mm, "mid": v(24.73, 11.4) * mm, "end": v(25.31, 13.05) * mm});
            skArc(sketch, "E45.19.13.0", {"start": v(21.48, 14.18) * mm, "mid": v(23.22, 14.23) * mm, "end": v(24.9, 13.8) * mm});
            skLineSegment(sketch, "E45.23.13.0", {"start": v(20.86, 13.94) * mm, "end": v(19.76, 13.2) * mm});
            skArc(sketch, "E45.26.13.0", {"start": v(23.17, 9.6) * mm, "mid": v(23.47, 9.76) * mm, "end": v(23.72, 9.98) * mm});
            skArc(sketch, "E45.30.13.0", {"start": v(21.48, 14.18) * mm, "mid": v(21.15, 14.1) * mm, "end": v(20.86, 13.94) * mm});
            skArc(sketch, "E45.34.13.0", {"start": v(25.31, 13.05) * mm, "mid": v(25.32, 13.2) * mm, "end": v(25.28, 13.34) * mm});
            skLineSegment(sketch, "E45.38.13.0", {"start": v(25.14, 13.61) * mm, "end": v(25.23, 13.48) * mm});
            skLineSegment(sketch, "E45.41.13.0", {"start": v(25.28, 13.34) * mm, "end": v(25.23, 13.48) * mm});
            skArc(sketch, "E45.44.13.0", {"start": v(25.14, 13.61) * mm, "mid": v(25.04, 13.72) * mm, "end": v(24.9, 13.8) * mm});
            skArc(sketch, "E45.2.14.0", {"start": v(11.09, 19.26) * mm, "mid": v(12.24, 19.1) * mm, "end": v(13.2, 19.76) * mm});
            skArc(sketch, "E45.4.14.0", {"start": v(16.8, 16.8) * mm, "mid": v(16.34, 15.73) * mm, "end": v(16.73, 14.63) * mm});
            skPoint(sketch, "E45.8.14.0", {"position": v(17.9, 22.28) * mm});
            skPoint(sketch, "E45.9.14.0", {"position": v(14.11, 21.12) * mm});
            skPoint(sketch, "E45.10.14.0", {"position": v(17.96, 17.96) * mm});
            skPoint(sketch, "E45.11.14.0", {"position": v(18.36, 21.9) * mm});
            skLineSegment(sketch, "E45.12.14.0", {"start": v(17.74, 17.74) * mm, "end": v(16.8, 16.8) * mm});
            skArc(sketch, "E45.15.14.0", {"start": v(18.1, 18.3) * mm, "mid": v(18.48, 20) * mm, "end": v(18.4, 21.74) * mm});
            skArc(sketch, "E45.19.14.0", {"start": v(14.42, 21.32) * mm, "mid": v(16, 22.03) * mm, "end": v(17.73, 22.28) * mm});
            skLineSegment(sketch, "E45.23.14.0", {"start": v(13.94, 20.86) * mm, "end": v(13.2, 19.76) * mm});
            skArc(sketch, "E45.26.14.0", {"start": v(17.74, 17.74) * mm, "mid": v(17.95, 18) * mm, "end": v(18.1, 18.3) * mm});
            skArc(sketch, "E45.30.14.0", {"start": v(14.42, 21.32) * mm, "mid": v(14.15, 21.11) * mm, "end": v(13.94, 20.86) * mm});
            skArc(sketch, "E45.34.14.0", {"start": v(18.4, 21.74) * mm, "mid": v(18.34, 21.88) * mm, "end": v(18.25, 22) * mm});
            skLineSegment(sketch, "E45.38.14.0", {"start": v(18.02, 22.2) * mm, "end": v(18.15, 22.11) * mm});
            skLineSegment(sketch, "E45.41.14.0", {"start": v(18.25, 22) * mm, "end": v(18.15, 22.11) * mm});
            skArc(sketch, "E45.44.14.0", {"start": v(18.02, 22.2) * mm, "mid": v(17.88, 22.26) * mm, "end": v(17.73, 22.28) * mm});
            skArc(sketch, "E45.2.15.0", {"start": v(2.87, 22.04) * mm, "mid": v(4, 22.32) * mm, "end": v(4.64, 23.3) * mm});
            skArc(sketch, "E45.4.15.0", {"start": v(9.1, 21.95) * mm, "mid": v(9.07, 20.79) * mm, "end": v(9.86, 19.92) * mm});
            skPoint(sketch, "E45.8.15.0", {"position": v(8, 27.43) * mm});
            skPoint(sketch, "E45.9.15.0", {"position": v(4.96, 24.91) * mm});
            skPoint(sketch, "E45.10.15.0", {"position": v(9.72, 23.47) * mm});
            skPoint(sketch, "E45.11.15.0", {"position": v(8.59, 27.25) * mm});
            skLineSegment(sketch, "E45.12.15.0", {"start": v(9.6, 23.17) * mm, "end": v(9.1, 21.95) * mm});
            skArc(sketch, "E45.15.15.0", {"start": v(9.72, 23.83) * mm, "mid": v(9.42, 25.55) * mm, "end": v(8.67, 27.12) * mm});
            skArc(sketch, "E45.19.15.0", {"start": v(5.16, 25.22) * mm, "mid": v(6.36, 26.48) * mm, "end": v(7.86, 27.37) * mm});
            skLineSegment(sketch, "E45.23.15.0", {"start": v(4.9, 24.6) * mm, "end": v(4.64, 23.3) * mm});
            skArc(sketch, "E45.26.15.0", {"start": v(9.6, 23.17) * mm, "mid": v(9.7, 23.5) * mm, "end": v(9.72, 23.83) * mm});
            skArc(sketch, "E45.30.15.0", {"start": v(5.16, 25.22) * mm, "mid": v(5, 24.92) * mm, "end": v(4.9, 24.6) * mm});
            skArc(sketch, "E45.34.15.0", {"start": v(8.67, 27.12) * mm, "mid": v(8.57, 27.24) * mm, "end": v(8.44, 27.31) * mm});
            skLineSegment(sketch, "E45.38.15.0", {"start": v(8.15, 27.4) * mm, "end": v(8.3, 27.37) * mm});
            skLineSegment(sketch, "E45.41.15.0", {"start": v(8.44, 27.31) * mm, "end": v(8.3, 27.37) * mm});
            skArc(sketch, "E45.44.15.0", {"start": v(8.15, 27.4) * mm, "mid": v(8, 27.4) * mm, "end": v(7.86, 27.37) * mm});
            skArc(sketch, "E46.trimOffspring", {"start": v(-13.55, 17.62) * mm, "mid": v(-14.1, 17.18) * mm, "end": v(-14.63, 16.73) * mm});
            skArc(sketch, "E47.trimOffspring", {"start": v(-19.26, 11.09) * mm, "mid": v(-19.6, 10.48) * mm, "end": v(-19.92, 9.86) * mm});
            skArc(sketch, "E48.trimOffspring", {"start": v(-22.04, 2.87) * mm, "mid": v(-22.12, 2.18) * mm, "end": v(-22.18, 1.48) * mm});
            skArc(sketch, "E49.trimOffspring", {"start": v(-21.46, -5.78) * mm, "mid": v(-21.27, -6.45) * mm, "end": v(-21.05, -7.12) * mm});
            skArc(sketch, "E50.trimOffspring", {"start": v(-17.62, -13.55) * mm, "mid": v(-17.18, -14.1) * mm, "end": v(-16.73, -14.63) * mm});
            skArc(sketch, "E51.trimOffspring", {"start": v(-11.09, -19.26) * mm, "mid": v(-10.48, -19.6) * mm, "end": v(-9.86, -19.92) * mm});
            skArc(sketch, "E52.trimOffspring", {"start": v(2.87, 22.04) * mm, "mid": v(2.18, 22.12) * mm, "end": v(1.48, 22.18) * mm});
            skArc(sketch, "E53.trimOffspring", {"start": v(11.09, 19.26) * mm, "mid": v(10.48, 19.6) * mm, "end": v(9.86, 19.92) * mm});
            skArc(sketch, "E54.trimOffspring", {"start": v(17.62, 13.55) * mm, "mid": v(17.18, 14.1) * mm, "end": v(16.73, 14.63) * mm});
            skArc(sketch, "E55.trimOffspring", {"start": v(21.46, 5.78) * mm, "mid": v(21.27, 6.45) * mm, "end": v(21.05, 7.12) * mm});
            skArc(sketch, "E56.trimOffspring", {"start": v(22.04, -2.87) * mm, "mid": v(22.12, -2.18) * mm, "end": v(22.18, -1.48) * mm});
            skArc(sketch, "E57.trimOffspring", {"start": v(19.26, -11.09) * mm, "mid": v(19.6, -10.48) * mm, "end": v(19.92, -9.86) * mm});
            skArc(sketch, "E58.trimOffspring", {"start": v(13.55, -17.62) * mm, "mid": v(14.1, -17.18) * mm, "end": v(14.63, -16.73) * mm});
            skArc(sketch, "E59.trimOffspring", {"start": v(5.78, -21.46) * mm, "mid": v(6.45, -21.27) * mm, "end": v(7.12, -21.05) * mm});
            skArc(sketch, "E60.trimOffspring", {"start": v(-2.87, -22.04) * mm, "mid": v(-2.18, -22.12) * mm, "end": v(-1.48, -22.18) * mm});
            skSolve(sketch);
        }
        {
            var Q0;
            Q0=makeQuery(id+"F0.imprint","IMPRINT",FACE,{"disambiguationData":[TD([[makeQuery(id+"F0.imprint","IMPRINT",EDGE,{"derivedFrom":sQuery(id+"F0.wireOp",EDGE,"E0")}),1.0]])]});
            var Q1;
            Q1=makeQuery(id+"F2.imprint","IMPRINT",FACE,{"disambiguationData":[TD([[makeQuery(id+"F2.imprint","IMPRINT",EDGE,{"derivedFrom":sQuery(id+"F2.wireOp",EDGE,"E30")}),1.0]])]});
            var Q2;
            Q2=sQuery(id+"F0.wireOp",VERTEX,"E14.47.15.0.end");
            var Q3;
            Q3=sQuery(id+"F2.wireOp",VERTEX,"E45.41.14.0.end");
            loft(context, id + "F3", {"sheetProfilesArray" : [{ "sheetProfileEntities" : qUnion([Q0]) }, { "sheetProfileEntities" : qUnion([Q1]) }], "matchConnections" : true, "connections" : [{ "connectionEntities" : qUnion([Q2, Q3]), "connectionEdgeQueries" : qUnion([]), "connectionEdgeParameters" : [] }]});
        }
        {
            var Q0;
            Q0=sQuery(id+"F2.wireOp",VERTEX,"E30.center");
            var Q1;
            Q1=makeQuery(id+"F3.opLoft","SWEPT_BODY",BODY,{"disambiguationData":[OSD([makeQuery(id+"F0.imprint","IMPRINT",FACE,{"disambiguationData":[TD([[makeQuery(id+"F0.imprint","IMPRINT",EDGE,{"derivedFrom":sQuery(id+"F0.wireOp",EDGE,"E0")}),1.0]])]}),makeQuery(id+"F2.imprint","IMPRINT",FACE,{"disambiguationData":[TD([[makeQuery(id+"F2.imprint","IMPRINT",EDGE,{"derivedFrom":sQuery(id+"F2.wireOp",EDGE,"E30")}),1.0]])]})])]});
            hole(context, id + "F4", {"style" : HoleStyle.SIMPLE, "endStyle" : HoleEndStyle.THROUGH, "holeDiameter" : 12.7 * mm, "tappedDepth" : 12.7 * mm, "tapClearance" : 3, "locations" : qUnion([Q0]), "scope" : qUnion([Q1])});
        }
    });
